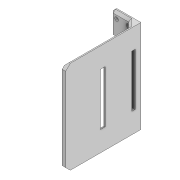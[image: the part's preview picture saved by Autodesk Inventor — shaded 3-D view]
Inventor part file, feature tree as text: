
AUTODESK INVENTOR PART (.ipt)
format: ipt  version: 2022 (Build 260153000, 153)  size: 270,336 bytes
history: native  units: mm
features: extrude x7, sketch x7, projected_geometry x4, chamfer x3, other x1
ambient origin geometry x8: Origin, YZ Plane, XZ Plane, XY Plane, X Axis, Y Axis, Z Axis, Center Point
bodies: Body1 (feature_tree)
feature tree (22):
  other  "Sólido1"
  extrude  "Extrusión1"  Depth=80.0mm
  extrude  "Extrusión2"  Depth=3.0mm
  extrude  "Extrusión3"  Depth=3.2mm
  extrude  "Extrusión4"  Depth=3.2mm
  extrude  "Extrusión5"  Depth=10.0mm
  chamfer  "Chaflán1"  Distance=5.0mm
  extrude  "Extrusión6"  Depth=2.0mm
  extrude  "Extrusión7"  Depth=35.0mm
  chamfer  "Chaflán4"  [1 undecoded]
  chamfer  "Chaflán5"  Distance=20.0mm
  sketch  "Boceto1"  dims[d0=20.0mm d1=80.0mm]
  sketch  "Boceto2"  dims[d2=3.0mm d3=0.0mm d4=3.2mm]
  projected_geometry  "Contorno proyectado1"
  sketch  "Boceto3"  dims[d7=3.2mm d9=3.2mm]
  projected_geometry  "Contorno proyectado2"
  sketch  "Boceto5"  dims[d10=3.2mm d11=3.2mm]
  projected_geometry  "Contorno proyectado3"
  sketch  "Boceto6"  dims[d12=3.2mm d13=10.0mm]
  projected_geometry  "Contorno proyectado4"
  sketch  "Boceto7"  dims[d14=10.0mm]
  sketch  "Boceto8"  dims[d15=10.0mm d16=5.0mm d17=70.0mm d18=35.0mm d19=0.0mm d20=0.0mm d21=20.0mm d22=20.0mm d23=30.0mm d24=15.0mm d26=5.0mm d27=0.0mm d28=0.0mm d29=3.0mm d30=35.0mm d31=0.0mm d32=2.0mm d33=3.0mm d34=45.0mm d35=22.5mm d37=26.0mm d38=3.0mm d39=1.5mm d40=0.0mm d41=0.0mm d42=4.9mm d43=2.0mm d44=45.0deg d45=7.0mm d46=7.0mm d47=7.0mm d48=7.0mm d49=10.0mm d50=0.0mm d57=30.0mm d58=3.0mm d59=0.0mm d60=4.0mm d61=2.0mm d62=45.0deg d63=2.0mm d64=2.0mm d65=45.0deg]
note: 1 required parameter value undecoded (feature->parameter linkage not recoverable at this tier; creation-order binding heuristic only, values carry confidence <= 0.55)
